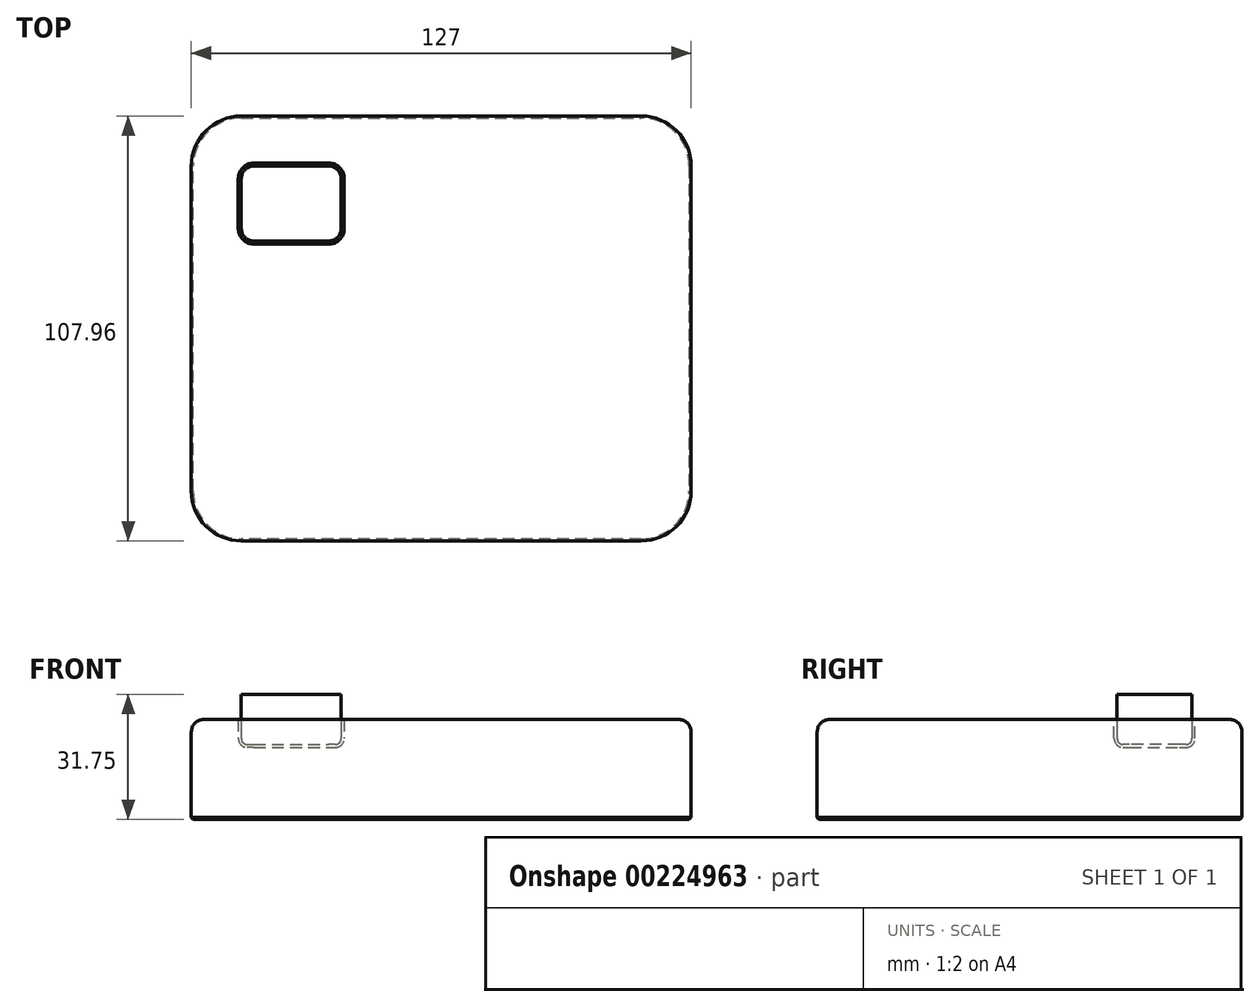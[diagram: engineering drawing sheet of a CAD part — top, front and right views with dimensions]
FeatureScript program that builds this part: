
annotation { "Feature Type Name" : "Feature", "Feature Type Description" : "" }
export const myFeature = defineFeature(function(context is Context, id is Id, definition is map)
    precondition{}
    {
        {
            var Q0;
            Q0=qCreatedBy(makeId("Top.planeOp"),FACE);
            var sketch = newSketch(context, id + "F0", { "sketchPlane" : qUnion([Q0])});
            skLineSegment(sketch, "E0.bottom", {"start": v(63.5, 53.98) * mm, "end": v(-63.5, 53.98) * mm});
            skLineSegment(sketch, "E0.top", {"start": v(63.5, -53.97) * mm, "end": v(-63.5, -53.97) * mm});
            skLineSegment(sketch, "E0.left", {"start": v(63.5, 53.98) * mm, "end": v(63.5, -53.98) * mm});
            skLineSegment(sketch, "E0.right", {"start": v(-63.5, 53.98) * mm, "end": v(-63.5, -53.97) * mm});
            skPoint(sketch, "E0.middle", {"position": v(0, 0) * mm});
            skSolve(sketch);
        }
        {
            var Q0;
            Q0=makeQuery(id+"F0.imprint","IMPRINT",FACE,{"disambiguationData":[TD([[makeQuery(id+"F0.imprint","IMPRINT",EDGE,{"derivedFrom":sQuery(id+"F0.wireOp",EDGE,"E0.bottom")}),1.0]])]});
            extrude(context, id + "F1", {"entities" : qUnion([Q0]), "depth" : 25.4 * mm});
        }
        {
            var Q0;
            Q0=makeQuery(id+"F1.opExtrude","CAP_FACE",FACE,{"disambiguationData":[OSD([sQuery(id+"F0.wireOp",EDGE,"E0.bottom"),sQuery(id+"F0.wireOp",EDGE,"E0.top"),sQuery(id+"F0.wireOp",EDGE,"E0.left"),sQuery(id+"F0.wireOp",EDGE,"E0.right")])],"isStart":false});
            var sketch = newSketch(context, id + "F2", { "sketchPlane" : qUnion([Q0])});
            skLineSegment(sketch, "E1.bottom", {"start": v(-50.8, 41.28) * mm, "end": v(-25.4, 41.28) * mm});
            skLineSegment(sketch, "E1.top", {"start": v(-50.8, 22.23) * mm, "end": v(-25.4, 22.23) * mm});
            skLineSegment(sketch, "E1.left", {"start": v(-50.8, 41.28) * mm, "end": v(-50.8, 22.23) * mm});
            skLineSegment(sketch, "E1.right", {"start": v(-25.4, 41.28) * mm, "end": v(-25.4, 22.23) * mm});
            skSolve(sketch);
        }
        {
            var Q0;
            Q0=qSketchRegion(id+"F2",true);
            extrude(context, id + "F3", {"entities" : qUnion([Q0]), "depth" : 12.7 * mm, "symmetric" : true});
        }
        {
            var Q0;
            Q0=makeQuery(id+"F3.opExtrude","SWEPT_EDGE",EDGE,{"disambiguationData":[OSD([sQuery(id+"F2.wireOp",EDGE,"E1.bottom"),sQuery(id+"F2.wireOp",EDGE,"E1.right")])]});
            var Q1;
            Q1=makeQuery(id+"F3.opExtrude","SWEPT_EDGE",EDGE,{"disambiguationData":[OSD([sQuery(id+"F2.wireOp",EDGE,"E1.top"),sQuery(id+"F2.wireOp",EDGE,"E1.right")])]});
            var Q2;
            Q2=makeQuery(id+"F3.opExtrude","SWEPT_EDGE",EDGE,{"disambiguationData":[OSD([sQuery(id+"F2.wireOp",EDGE,"E1.top"),sQuery(id+"F2.wireOp",EDGE,"E1.left")])]});
            var Q3;
            Q3=makeQuery(id+"F3.opExtrude","SWEPT_EDGE",EDGE,{"disambiguationData":[OSD([sQuery(id+"F2.wireOp",EDGE,"E1.bottom"),sQuery(id+"F2.wireOp",EDGE,"E1.left")])]});
            fillet(context, id + "F4", {"entities" : qUnion([Q0, Q1, Q2, Q3]), "radius" : 3.17 * mm, "tangentPropagation" : true, "allowEdgeOverflow" : false});
        }
        {
            var Q0;
            Q0=makeQuery(id+"F3.opExtrude","CAP_EDGE",EDGE,{"disambiguationData":[OSD([sQuery(id+"F2.wireOp",EDGE,"E1.top")])],"isStart":true});
            fillet(context, id + "F5", {"entities" : qUnion([Q0]), "radius" : 1.52 * mm, "tangentPropagation" : true, "allowEdgeOverflow" : false});
        }
        {
            var Q0;
            Q0=makeQuery(id+"F1.opExtrude","SWEPT_EDGE",EDGE,{"disambiguationData":[OSD([sQuery(id+"F0.wireOp",EDGE,"E0.top"),sQuery(id+"F0.wireOp",EDGE,"E0.left")])]});
            var Q1;
            Q1=makeQuery(id+"F1.opExtrude","SWEPT_EDGE",EDGE,{"disambiguationData":[OSD([sQuery(id+"F0.wireOp",EDGE,"E0.bottom"),sQuery(id+"F0.wireOp",EDGE,"E0.left")])]});
            var Q2;
            Q2=makeQuery(id+"F1.opExtrude","SWEPT_EDGE",EDGE,{"disambiguationData":[OSD([sQuery(id+"F0.wireOp",EDGE,"E0.bottom"),sQuery(id+"F0.wireOp",EDGE,"E0.right")])]});
            var Q3;
            Q3=makeQuery(id+"F1.opExtrude","SWEPT_EDGE",EDGE,{"disambiguationData":[OSD([sQuery(id+"F0.wireOp",EDGE,"E0.top"),sQuery(id+"F0.wireOp",EDGE,"E0.right")])]});
            fillet(context, id + "F6", {"entities" : qUnion([Q0, Q1, Q2, Q3]), "radius" : 12.7 * mm, "tangentPropagation" : true, "allowEdgeOverflow" : false});
        }
        {
            var Q0;
            Q0=makeQuery(id+"F1.opExtrude","CAP_EDGE",EDGE,{"disambiguationData":[OSD([sQuery(id+"F0.wireOp",EDGE,"E0.top")])],"isStart":false});
            fillet(context, id + "F7", {"entities" : qUnion([Q0]), "radius" : 3.17 * mm, "tangentPropagation" : true, "allowEdgeOverflow" : false});
        }
        {
            var Q0;
            Q0=makeQuery(id+"F1.opExtrude","CAP_EDGE",EDGE,{"disambiguationData":[OSD([sQuery(id+"F0.wireOp",EDGE,"E0.top")])],"isStart":true});
            chamfer(context, id + "F8", {"entities" : qUnion([Q0]), "width" : 0.5 * mm, "tangentPropagation" : true});
        }
        {
            var Q0;
            Q0=makeQuery(id+"F3.opExtrude","SWEPT_BODY",BODY,{"disambiguationData":[OSD([sQuery(id+"F2.wireOp",EDGE,"E1.bottom"),sQuery(id+"F2.wireOp",EDGE,"E1.top"),sQuery(id+"F2.wireOp",EDGE,"E1.left"),sQuery(id+"F2.wireOp",EDGE,"E1.right")])]});
            var Q1;
            Q1=makeQuery(id+"F1.opExtrude","SWEPT_BODY",BODY,{"disambiguationData":[OSD([sQuery(id+"F0.wireOp",EDGE,"E0.bottom"),sQuery(id+"F0.wireOp",EDGE,"E0.top"),sQuery(id+"F0.wireOp",EDGE,"E0.left"),sQuery(id+"F0.wireOp",EDGE,"E0.right")])]});
            booleanBodies(context, id + "F9", {"operationType" : BooleanOperationType.SUBTRACTION, "tools" : qUnion([Q0]), "targets" : qUnion([Q1]), "offset" : true, "offsetAll" : true, "offsetDistance" : 0.5 * mm, "keepTools" : true});
        }
        {
            var Q0;
            Q0=makeQuery(id+"F3.opExtrude","SWEPT_BODY",BODY,{"disambiguationData":[OSD([sQuery(id+"F2.wireOp",EDGE,"E1.bottom"),sQuery(id+"F2.wireOp",EDGE,"E1.top"),sQuery(id+"F2.wireOp",EDGE,"E1.left"),sQuery(id+"F2.wireOp",EDGE,"E1.right")])]});
            var Q1;
            Q1=makeQuery(id+"F1.opExtrude","SWEPT_BODY",BODY,{"disambiguationData":[OSD([sQuery(id+"F0.wireOp",EDGE,"E0.bottom"),sQuery(id+"F0.wireOp",EDGE,"E0.top"),sQuery(id+"F0.wireOp",EDGE,"E0.left"),sQuery(id+"F0.wireOp",EDGE,"E0.right")])]});
            booleanBodies(context, id + "F10", {"operationType" : BooleanOperationType.SUBTRACTION, "tools" : qUnion([Q0]), "targets" : qUnion([Q1]), "offset" : true, "offsetAll" : true, "offsetDistance" : 0.76 * mm, "keepTools" : true});
        }
    });
